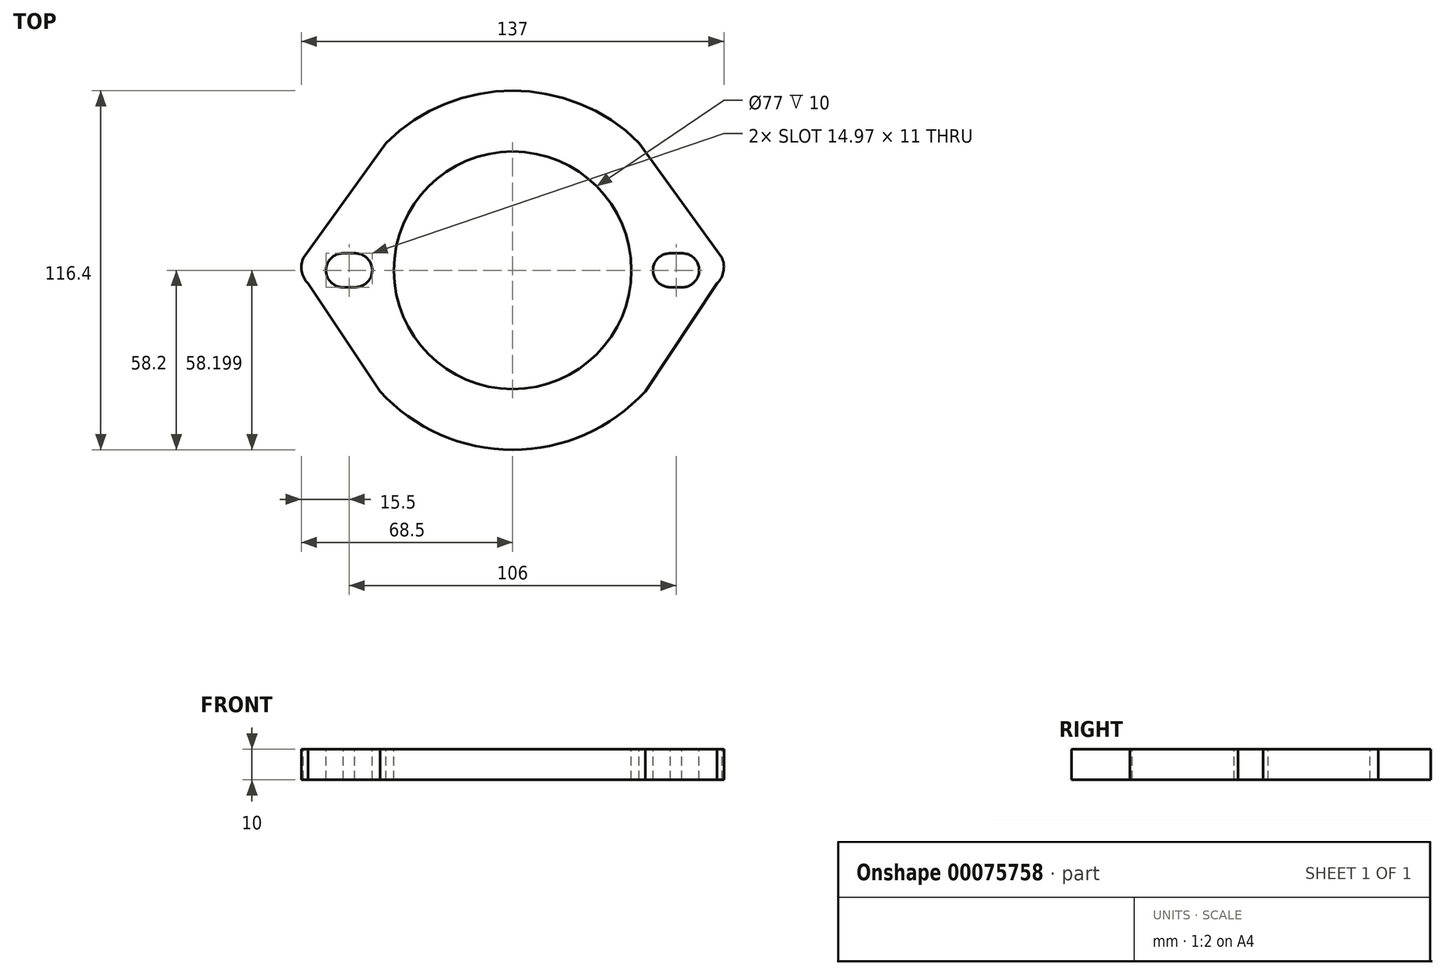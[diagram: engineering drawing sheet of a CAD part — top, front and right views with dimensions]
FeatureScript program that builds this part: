
annotation { "Feature Type Name" : "Feature", "Feature Type Description" : "" }
export const myFeature = defineFeature(function(context is Context, id is Id, definition is map)
    precondition{}
    {
        {
            var Q0;
            Q0=qCreatedBy(makeId("Top.planeOp"),FACE);
            var sketch = newSketch(context, id + "F0", { "sketchPlane" : qUnion([Q0])});
            skPoint(sketch, "E0.start.orphan", {"position": v(58.2, 0) * mm});
            skPoint(sketch, "E1.start.orphan", {"position": v(38.5, 0) * mm});
            skPoint(sketch, "E2.start.orphan", {"position": v(-38.5, 0) * mm});
            skArc(sketch, "E3", {"start": v(-42.98, -39.24) * mm, "mid": v(-23.38, -53.3) * mm, "end": v(0.23, -58.2) * mm});
            skArc(sketch, "E4", {"start": v(-65.97, 6.64) * mm, "mid": v(-68.5, 1.24) * mm, "end": v(-66.29, -4.3) * mm});
            skLineSegment(sketch, "E5", {"start": v(-67.9, 3.96) * mm, "end": v(-41.05, 41.25) * mm});
            skLineSegment(sketch, "E6", {"start": v(-66.29, -4.3) * mm, "end": v(-42.98, -39.24) * mm});
            skArc(sketch, "E7.trimOffspring", {"start": v(0.24, 58.2) * mm, "mid": v(-22.1, 53.84) * mm, "end": v(-41.05, 41.25) * mm});
            skArc(sketch, "E8", {"start": v(-54.94, 5.5) * mm, "mid": v(-60.49, -0.02) * mm, "end": v(-54.9, -5.5) * mm});
            skArc(sketch, "E9", {"start": v(-51.01, -5.5) * mm, "mid": v(-45.51, 0.07) * mm, "end": v(-51.15, 5.5) * mm});
            skLineSegment(sketch, "E10", {"start": v(-55.03, 5.5) * mm, "end": v(-50.88, 5.5) * mm});
            skLineSegment(sketch, "E11", {"start": v(-54.9, -5.5) * mm, "end": v(-51.01, -5.5) * mm});
            skArc(sketch, "E12", {"start": v(51, 5.5) * mm, "mid": v(51, 5.5) * mm, "end": v(51, 5.5) * mm});
            skLineSegment(sketch, "E13", {"start": v(51, 5.5) * mm, "end": v(51, 5.5) * mm});
            skLineSegment(sketch, "E14.MirrorCS", {"start": v(67.9, 3.96) * mm, "end": v(65.97, 6.64) * mm});
            skArc(sketch, "E15.MirrorCS", {"start": v(65.97, 6.64) * mm, "mid": v(67.09, 5.4) * mm, "end": v(67.9, 3.96) * mm});
            skPoint(sketch, "E16.startSnap0", {"position": v(-0.24, 58.2) * mm});
            skPoint(sketch, "E17.orphan", {"position": v(41.05, 41.25) * mm});
            skArc(sketch, "E18.trimOffspring", {"start": v(51, -5.5) * mm, "mid": v(51.02, -5.5) * mm, "end": v(51.05, -5.5) * mm});
            skPoint(sketch, "E19.center.orphan", {"position": v(55.01, 0) * mm});
            skPoint(sketch, "E20.orphan", {"position": v(55.01, 5.5) * mm});
            skPoint(sketch, "E21.orphan", {"position": v(66.29, -4.3) * mm});
            skLineSegment(sketch, "E22.MirrorCS", {"start": v(54.9, -5.5) * mm, "end": v(51.01, -5.5) * mm});
            skLineSegment(sketch, "E23.MirrorCS", {"start": v(55.03, 5.5) * mm, "end": v(50.88, 5.5) * mm});
            skArc(sketch, "E24.MirrorCS", {"start": v(54.94, 5.5) * mm, "mid": v(60.49, -0.02) * mm, "end": v(54.9, -5.5) * mm});
            skArc(sketch, "E25.MirrorCS", {"start": v(51.01, -5.5) * mm, "mid": v(45.51, 0.07) * mm, "end": v(51.15, 5.5) * mm});
            skArc(sketch, "E26.MirrorCS", {"start": v(65.97, 6.64) * mm, "mid": v(68.5, 1.24) * mm, "end": v(66.29, -4.3) * mm});
            skLineSegment(sketch, "E27.MirrorCS", {"start": v(66.29, -4.3) * mm, "end": v(42.98, -39.24) * mm});
            skLineSegment(sketch, "E28.MirrorCS", {"start": v(67.9, 3.96) * mm, "end": v(41.05, 41.25) * mm});
            skArc(sketch, "E29.MirrorCS", {"start": v(-0.24, 58.2) * mm, "mid": v(22.1, 53.84) * mm, "end": v(41.05, 41.25) * mm});
            skArc(sketch, "E30.MirrorCS", {"start": v(42.98, -39.24) * mm, "mid": v(23.38, -53.3) * mm, "end": v(-0.23, -58.2) * mm});
            skCircle(sketch, "E31", {"center": v(0, 0) * mm, "radius": 38.5 * mm});
            skSolve(sketch);
        }
        {
            var Q0;
            Q0=makeQuery(id+"F0.imprint","IMPRINT",FACE,{"disambiguationData":[TD([[makeQuery(id+"F0.imprint","IMPRINT",EDGE,{"derivedFrom":sQuery(id+"F0.wireOp",EDGE,"35QTtZPc-dBJe-AFMl-doRS-0cuBAvYJZLRc")}),-1.0]])]});
            var Q1;
            {var subQ28=sQuery(id+"F0.wireOp",EDGE,"E3");Q1=makeQuery(id+"F0.imprint","IMPRINT",FACE,{"disambiguationData":[TD([[makeQuery(id+"F0.imprint","IMPRINT",EDGE,{"derivedFrom":subQ28}),1.0]])]});}
            extrude(context, id + "F1", {"entities" : qUnion([Q0, Q1]), "oppositeDirection" : true, "depth" : 10 * mm});
        }
    });
